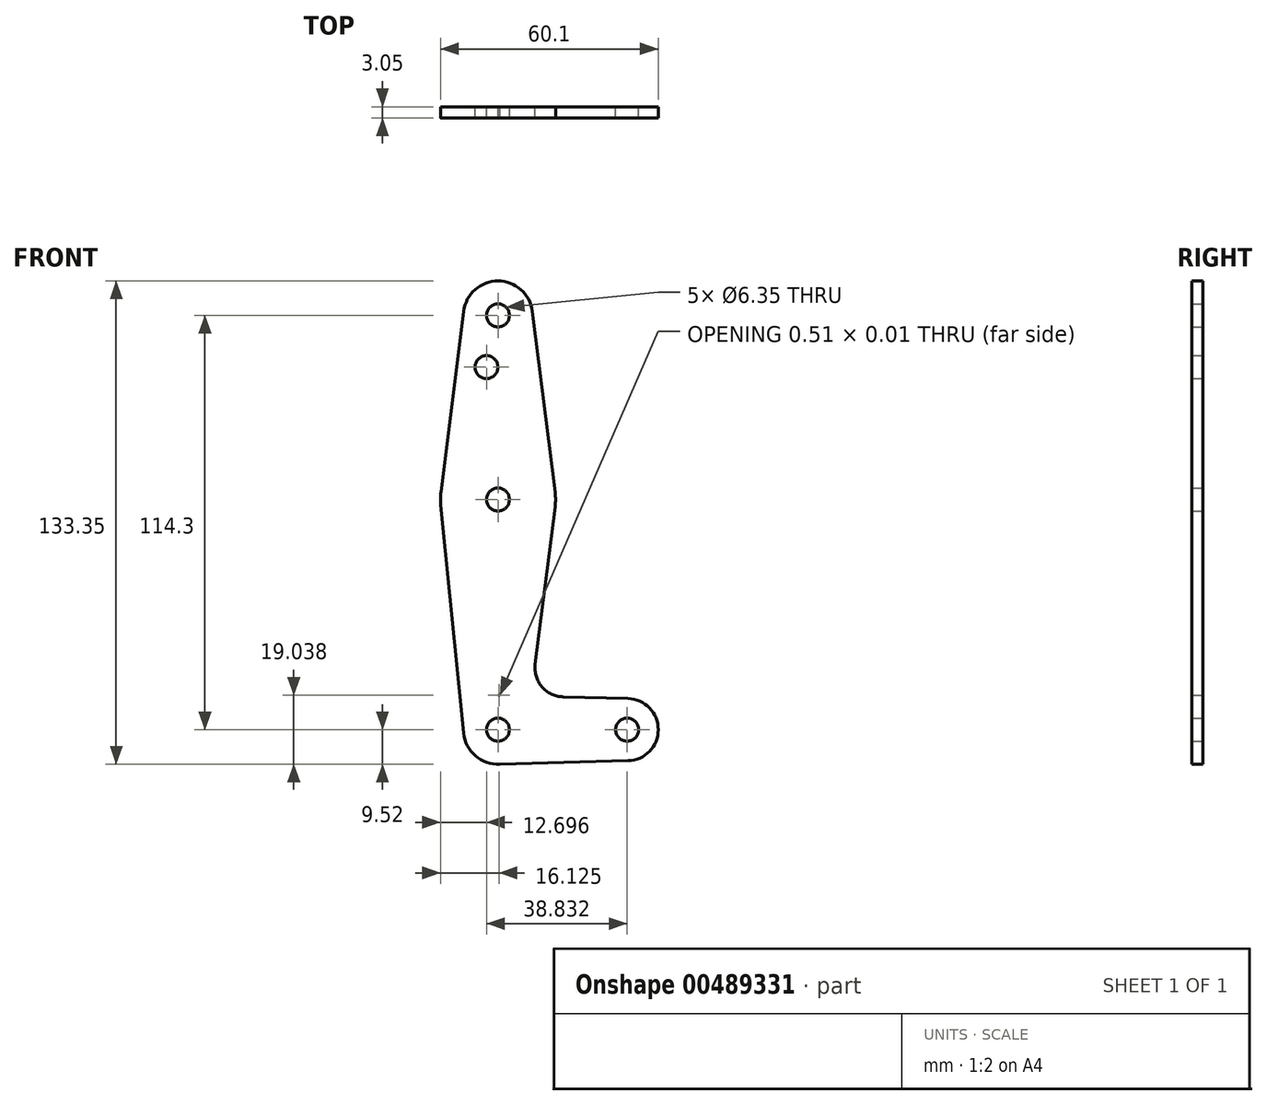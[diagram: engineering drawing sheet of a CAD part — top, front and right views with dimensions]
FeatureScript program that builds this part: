
annotation { "Feature Type Name" : "Feature", "Feature Type Description" : "" }
export const myFeature = defineFeature(function(context is Context, id is Id, definition is map)
    precondition{}
    {
        {
            var Q0;
            Q0=qCreatedBy(makeId("Front.planeOp"),FACE);
            var sketch = newSketch(context, id + "F0", { "sketchPlane" : qUnion([Q0])});
            skLineSegment(sketch, "E0", {"start": v(-17.07, 95.93) * mm, "end": v(-17.07, -18.37) * mm, "construction": true});
            skCircle(sketch, "E1", {"center": v(-17.07, 95.93) * mm, "radius": 9.53 * mm});
            skCircle(sketch, "E2", {"center": v(-17.07, 45.13) * mm, "radius": 15.88 * mm});
            skCircle(sketch, "E3", {"center": v(-17.07, -18.37) * mm, "radius": 9.53 * mm});
            skPoint(sketch, "E4.center.orphan", {"position": v(13.7, -18.37) * mm});
            skPoint(sketch, "E5.orphan", {"position": v(18.59, -18.37) * mm});
            skLineSegment(sketch, "E6", {"start": v(-17.07, -18.37) * mm, "end": v(18.59, -18.37) * mm, "construction": true});
            skCircle(sketch, "E7", {"center": v(18.59, -18.37) * mm, "radius": 8.57 * mm});
            skLineSegment(sketch, "E8", {"start": v(-26.52, 97.12) * mm, "end": v(-32.82, 47.11) * mm});
            skLineSegment(sketch, "E9", {"start": v(-7.62, 97.12) * mm, "end": v(-1.32, 47.11) * mm});
            skLineSegment(sketch, "E10", {"start": v(-1.32, 47.11) * mm, "end": v(-1.32, 43.15) * mm});
            skLineSegment(sketch, "E11", {"start": v(-1.32, 43.15) * mm, "end": v(-6.8, -0.38) * mm});
            skLineSegment(sketch, "E12", {"start": v(-17.07, -8.84) * mm, "end": v(-16.56, -8.86) * mm});
            skLineSegment(sketch, "E13", {"start": v(-17.07, -27.9) * mm, "end": v(18.82, -26.94) * mm});
            skLineSegment(sketch, "E14", {"start": v(-32.82, 47.11) * mm, "end": v(-32.86, 43.54) * mm});
            skCircle(sketch, "E15", {"center": v(-17.07, 95.93) * mm, "radius": 3.18 * mm});
            skCircle(sketch, "E16", {"center": v(-17.07, 45.13) * mm, "radius": 3.18 * mm});
            skCircle(sketch, "E17", {"center": v(-17.07, -18.37) * mm, "radius": 3.18 * mm});
            skCircle(sketch, "E18", {"center": v(18.59, -18.37) * mm, "radius": 3.18 * mm});
            skCircle(sketch, "E19", {"center": v(-20.24, 81.66) * mm, "radius": 3.18 * mm});
            skArc(sketch, "E20", {"start": v(-6.8, -0.38) * mm, "mid": v(-4.95, -6.55) * mm, "end": v(0.87, -9.32) * mm});
            skLineSegment(sketch, "E21.trimOffspring", {"start": v(0.87, -9.32) * mm, "end": v(18.82, -9.8) * mm});
            skPoint(sketch, "E22.end.orphan", {"position": v(-26.64, -18.37) * mm});
            skLineSegment(sketch, "E23", {"start": v(-26.55, -19.32) * mm, "end": v(-32.86, 43.54) * mm});
            skLineSegment(sketch, "E24", {"start": v(-32.86, 43.54) * mm, "end": v(-32.82, 47.11) * mm});
            skSolve(sketch);
        }
        {
            var Q0;
            Q0 = qSketchRegion(id + "F0", true);
            extrude(context, id + "F1", {"entities" : qUnion([Q0]), "depth" : 3.05 * mm});
        }
    });
